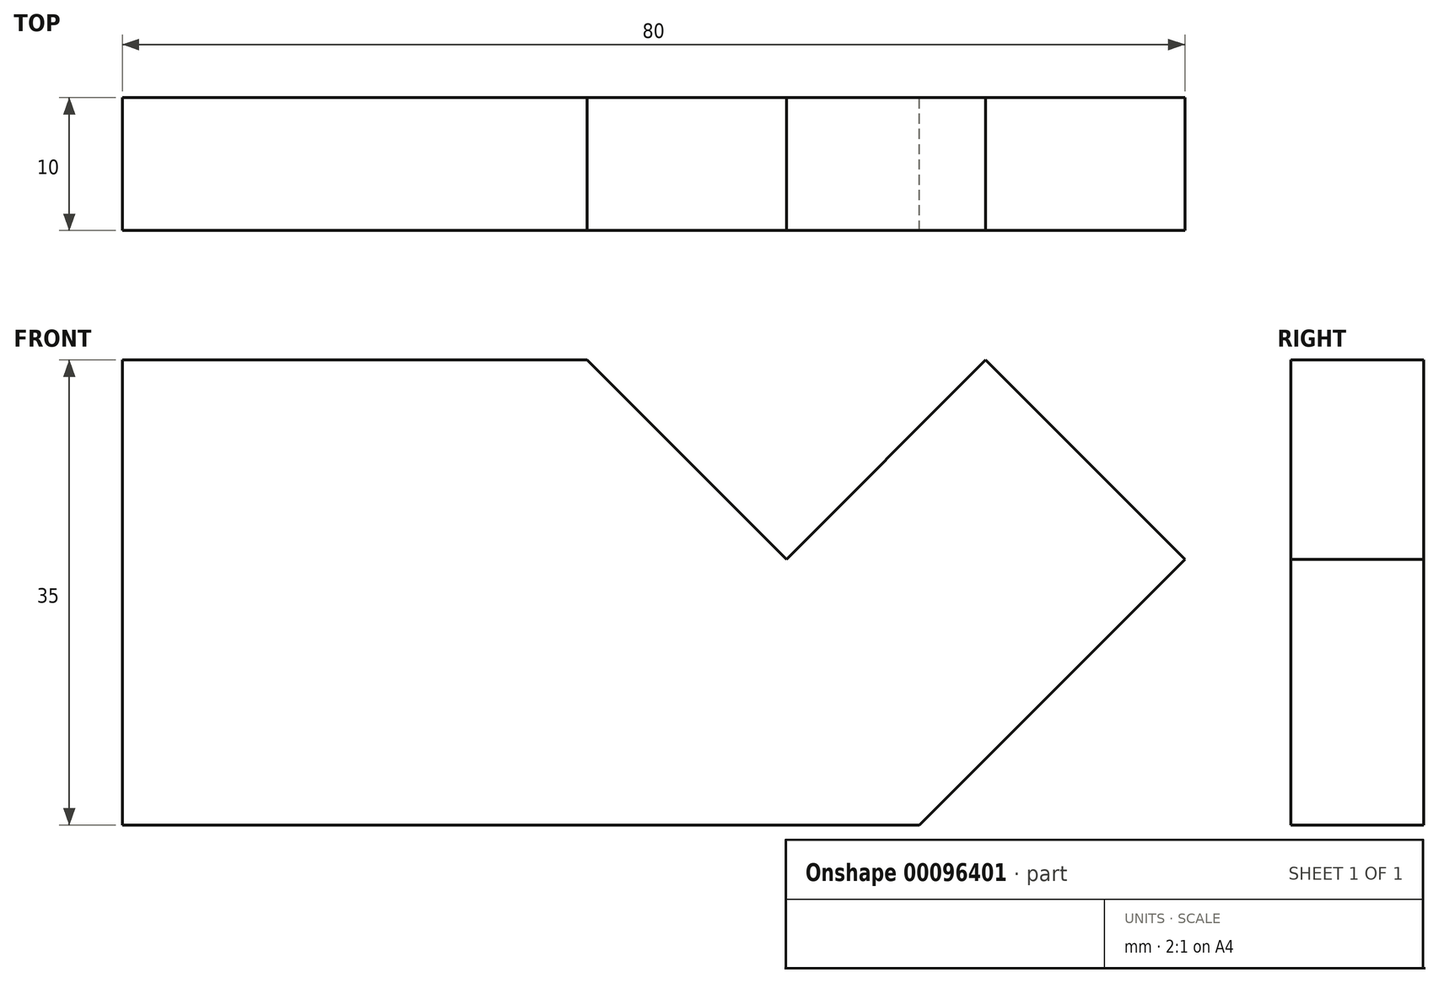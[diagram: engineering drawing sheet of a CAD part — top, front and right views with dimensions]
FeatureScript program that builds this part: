
annotation { "Feature Type Name" : "Feature", "Feature Type Description" : "" }
export const myFeature = defineFeature(function(context is Context, id is Id, definition is map)
    precondition{}
    {
        {
            var Q0;
            Q0=qCreatedBy(makeId("Front.planeOp"),FACE);
            var sketch = newSketch(context, id + "F0", { "sketchPlane" : qUnion([Q0])});
            skLineSegment(sketch, "E0", {"start": v(0, 0) * mm, "end": v(0, 35) * mm});
            skLineSegment(sketch, "E1", {"start": v(0, 0) * mm, "end": v(60, 0) * mm});
            skLineSegment(sketch, "E2", {"start": v(0, 35) * mm, "end": v(35, 35) * mm});
            skLineSegment(sketch, "E3", {"start": v(60, 0) * mm, "end": v(80, 20) * mm});
            skLineSegment(sketch, "E4", {"start": v(80, 20) * mm, "end": v(65, 35) * mm});
            skLineSegment(sketch, "E5", {"start": v(65, 35) * mm, "end": v(50, 20) * mm});
            skLineSegment(sketch, "E6", {"start": v(50, 20) * mm, "end": v(35, 35) * mm});
            skSolve(sketch);
        }
        {
            var Q0;
            Q0 = qSketchRegion(id + "F0", true);
            extrude(context, id + "F1", {"entities" : qUnion([Q0]), "depth" : 10 * mm});
        }
    });
